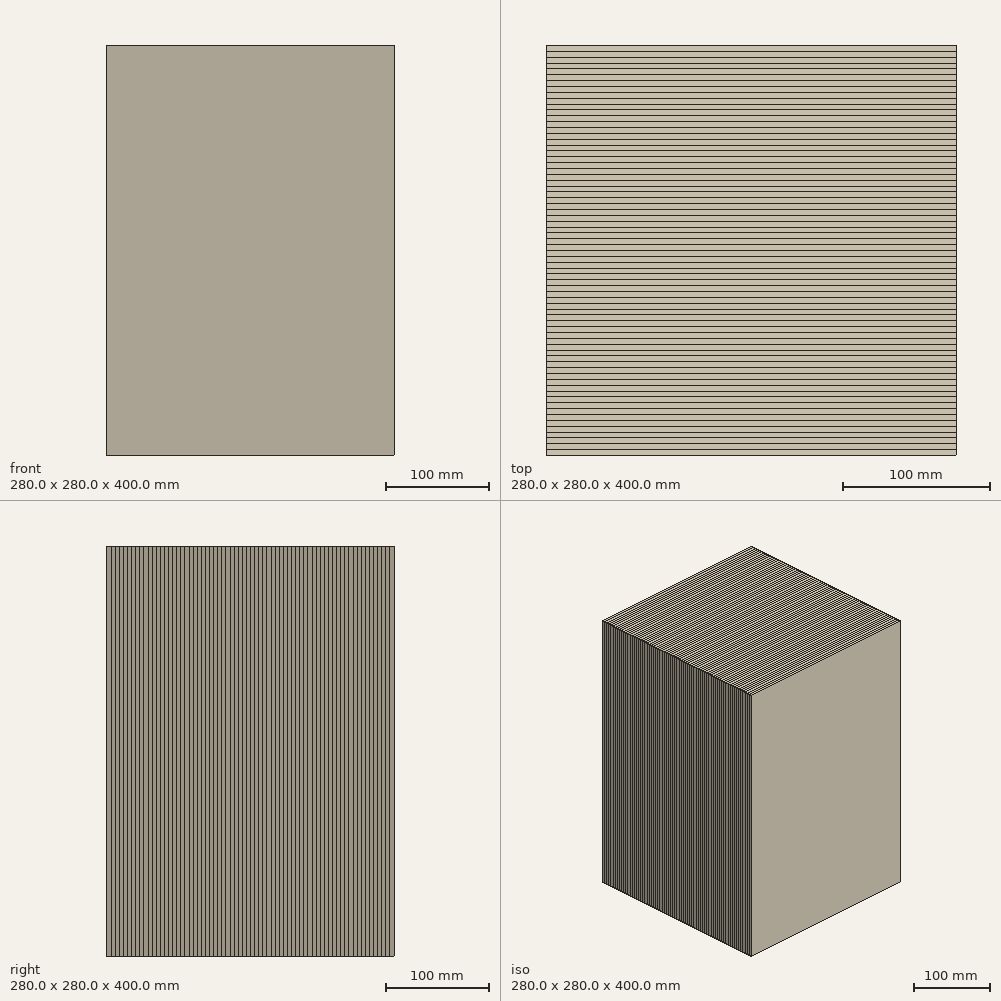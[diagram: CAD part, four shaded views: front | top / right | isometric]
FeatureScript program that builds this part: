
annotation { "Feature Type Name" : "Feature", "Feature Type Description" : "" }
export const myFeature = defineFeature(function(context is Context, id is Id, definition is map)
    precondition{}
    {
        {
            var Q0;
            Q0=qCreatedBy(makeId("Top.planeOp"),FACE);
            var sketch = newSketch(context, id + "F0", { "sketchPlane" : qUnion([Q0])});
            skLineSegment(sketch, "E0.bottom", {"start": v(-140, -140) * mm, "end": v(140, -140) * mm});
            skLineSegment(sketch, "E0.top", {"start": v(-140, 140) * mm, "end": v(140, 140) * mm});
            skLineSegment(sketch, "E0.left", {"start": v(-140, -140) * mm, "end": v(-140, 140) * mm});
            skLineSegment(sketch, "E0.right", {"start": v(140, -140) * mm, "end": v(140, 140) * mm});
            skPoint(sketch, "E0.middle", {"position": v(0, 0) * mm});
            skSolve(sketch);
        }
        {
            var Q0;
            Q0 = qSketchRegion(id + "F0", true);
            extrude(context, id + "F1", {"entities" : qUnion([Q0]), "depth" : 400 * mm, "offsetDistance" : 25 * mm});
        }
        {
            var Q0;
            Q0=makeQuery(id+"F1.opExtrude","SWEPT_FACE",FACE,{"disambiguationData":[OSD([sQuery(id+"F0.wireOp",EDGE,"E0.right")])]});
            var sketch = newSketch(context, id + "F2", { "sketchPlane" : qUnion([Q0])});
            skLineSegment(sketch, "E1.bottom", {"start": v(-140, 400) * mm, "end": v(-136, 400) * mm});
            skLineSegment(sketch, "E1.top", {"start": v(-140, 0) * mm, "end": v(-136, 0) * mm});
            skLineSegment(sketch, "E1.left", {"start": v(-140, 400) * mm, "end": v(-140, 0) * mm});
            skLineSegment(sketch, "E1.right", {"start": v(-136, 400) * mm, "end": v(-136, 0) * mm});
            skLineSegment(sketch, "E2.1.0.0", {"start": v(-132, 400) * mm, "end": v(-132, 0) * mm});
            skLineSegment(sketch, "E2.1.0.1", {"start": v(-128, 400) * mm, "end": v(-128, 0) * mm});
            skLineSegment(sketch, "E2.1.0.2", {"start": v(-132, 400) * mm, "end": v(-128, 400) * mm});
            skLineSegment(sketch, "E2.1.0.3", {"start": v(-132, 0) * mm, "end": v(-128, 0) * mm});
            skLineSegment(sketch, "E2.2.0.0", {"start": v(-124, 400) * mm, "end": v(-124, 0) * mm});
            skLineSegment(sketch, "E2.2.0.1", {"start": v(-120, 400) * mm, "end": v(-120, 0) * mm});
            skLineSegment(sketch, "E2.2.0.2", {"start": v(-124, 400) * mm, "end": v(-120, 400) * mm});
            skLineSegment(sketch, "E2.2.0.3", {"start": v(-124, 0) * mm, "end": v(-120, 0) * mm});
            skLineSegment(sketch, "E2.3.0.0", {"start": v(-116, 400) * mm, "end": v(-116, 0) * mm});
            skLineSegment(sketch, "E2.3.0.1", {"start": v(-112, 400) * mm, "end": v(-112, 0) * mm});
            skLineSegment(sketch, "E2.3.0.2", {"start": v(-116, 400) * mm, "end": v(-112, 400) * mm});
            skLineSegment(sketch, "E2.3.0.3", {"start": v(-116, 0) * mm, "end": v(-112, 0) * mm});
            skLineSegment(sketch, "E2.4.0.0", {"start": v(-108, 400) * mm, "end": v(-108, 0) * mm});
            skLineSegment(sketch, "E2.4.0.1", {"start": v(-104, 400) * mm, "end": v(-104, 0) * mm});
            skLineSegment(sketch, "E2.4.0.2", {"start": v(-108, 400) * mm, "end": v(-104, 400) * mm});
            skLineSegment(sketch, "E2.4.0.3", {"start": v(-108, 0) * mm, "end": v(-104, 0) * mm});
            skLineSegment(sketch, "E2.5.0.0", {"start": v(-100, 400) * mm, "end": v(-100, 0) * mm});
            skLineSegment(sketch, "E2.5.0.1", {"start": v(-96, 400) * mm, "end": v(-96, 0) * mm});
            skLineSegment(sketch, "E2.5.0.2", {"start": v(-100, 400) * mm, "end": v(-96, 400) * mm});
            skLineSegment(sketch, "E2.5.0.3", {"start": v(-100, 0) * mm, "end": v(-96, 0) * mm});
            skLineSegment(sketch, "E2.6.0.0", {"start": v(-92, 400) * mm, "end": v(-92, 0) * mm});
            skLineSegment(sketch, "E2.6.0.1", {"start": v(-88, 400) * mm, "end": v(-88, 0) * mm});
            skLineSegment(sketch, "E2.6.0.2", {"start": v(-92, 400) * mm, "end": v(-88, 400) * mm});
            skLineSegment(sketch, "E2.6.0.3", {"start": v(-92, 0) * mm, "end": v(-88, 0) * mm});
            skLineSegment(sketch, "E2.7.0.0", {"start": v(-84, 400) * mm, "end": v(-84, 0) * mm});
            skLineSegment(sketch, "E2.7.0.1", {"start": v(-80, 400) * mm, "end": v(-80, 0) * mm});
            skLineSegment(sketch, "E2.7.0.2", {"start": v(-84, 400) * mm, "end": v(-80, 400) * mm});
            skLineSegment(sketch, "E2.7.0.3", {"start": v(-84, 0) * mm, "end": v(-80, 0) * mm});
            skLineSegment(sketch, "E2.8.0.0", {"start": v(-76, 400) * mm, "end": v(-76, 0) * mm});
            skLineSegment(sketch, "E2.8.0.1", {"start": v(-72, 400) * mm, "end": v(-72, 0) * mm});
            skLineSegment(sketch, "E2.8.0.2", {"start": v(-76, 400) * mm, "end": v(-72, 400) * mm});
            skLineSegment(sketch, "E2.8.0.3", {"start": v(-76, 0) * mm, "end": v(-72, 0) * mm});
            skLineSegment(sketch, "E2.9.0.0", {"start": v(-68, 400) * mm, "end": v(-68, 0) * mm});
            skLineSegment(sketch, "E2.9.0.1", {"start": v(-64, 400) * mm, "end": v(-64, 0) * mm});
            skLineSegment(sketch, "E2.9.0.2", {"start": v(-68, 400) * mm, "end": v(-64, 400) * mm});
            skLineSegment(sketch, "E2.9.0.3", {"start": v(-68, 0) * mm, "end": v(-64, 0) * mm});
            skLineSegment(sketch, "E2.10.0.0", {"start": v(-60, 400) * mm, "end": v(-60, 0) * mm});
            skLineSegment(sketch, "E2.10.0.1", {"start": v(-56, 400) * mm, "end": v(-56, 0) * mm});
            skLineSegment(sketch, "E2.10.0.2", {"start": v(-60, 400) * mm, "end": v(-56, 400) * mm});
            skLineSegment(sketch, "E2.10.0.3", {"start": v(-60, 0) * mm, "end": v(-56, 0) * mm});
            skLineSegment(sketch, "E2.11.0.0", {"start": v(-52, 400) * mm, "end": v(-52, 0) * mm});
            skLineSegment(sketch, "E2.11.0.1", {"start": v(-48, 400) * mm, "end": v(-48, 0) * mm});
            skLineSegment(sketch, "E2.11.0.2", {"start": v(-52, 400) * mm, "end": v(-48, 400) * mm});
            skLineSegment(sketch, "E2.11.0.3", {"start": v(-52, 0) * mm, "end": v(-48, 0) * mm});
            skLineSegment(sketch, "E2.12.0.0", {"start": v(-44, 400) * mm, "end": v(-44, 0) * mm});
            skLineSegment(sketch, "E2.12.0.1", {"start": v(-40, 400) * mm, "end": v(-40, 0) * mm});
            skLineSegment(sketch, "E2.12.0.2", {"start": v(-44, 400) * mm, "end": v(-40, 400) * mm});
            skLineSegment(sketch, "E2.12.0.3", {"start": v(-44, 0) * mm, "end": v(-40, 0) * mm});
            skLineSegment(sketch, "E2.13.0.0", {"start": v(-36, 400) * mm, "end": v(-36, 0) * mm});
            skLineSegment(sketch, "E2.13.0.1", {"start": v(-32, 400) * mm, "end": v(-32, 0) * mm});
            skLineSegment(sketch, "E2.13.0.2", {"start": v(-36, 400) * mm, "end": v(-32, 400) * mm});
            skLineSegment(sketch, "E2.13.0.3", {"start": v(-36, 0) * mm, "end": v(-32, 0) * mm});
            skLineSegment(sketch, "E2.14.0.0", {"start": v(-28, 400) * mm, "end": v(-28, 0) * mm});
            skLineSegment(sketch, "E2.14.0.1", {"start": v(-24, 400) * mm, "end": v(-24, 0) * mm});
            skLineSegment(sketch, "E2.14.0.2", {"start": v(-28, 400) * mm, "end": v(-24, 400) * mm});
            skLineSegment(sketch, "E2.14.0.3", {"start": v(-28, 0) * mm, "end": v(-24, 0) * mm});
            skLineSegment(sketch, "E2.15.0.0", {"start": v(-20, 400) * mm, "end": v(-20, 0) * mm});
            skLineSegment(sketch, "E2.15.0.1", {"start": v(-16, 400) * mm, "end": v(-16, 0) * mm});
            skLineSegment(sketch, "E2.15.0.2", {"start": v(-20, 400) * mm, "end": v(-16, 400) * mm});
            skLineSegment(sketch, "E2.15.0.3", {"start": v(-20, 0) * mm, "end": v(-16, 0) * mm});
            skLineSegment(sketch, "E2.16.0.0", {"start": v(-12, 400) * mm, "end": v(-12, 0) * mm});
            skLineSegment(sketch, "E2.16.0.1", {"start": v(-8, 400) * mm, "end": v(-8, 0) * mm});
            skLineSegment(sketch, "E2.16.0.2", {"start": v(-12, 400) * mm, "end": v(-8, 400) * mm});
            skLineSegment(sketch, "E2.16.0.3", {"start": v(-12, 0) * mm, "end": v(-8, 0) * mm});
            skLineSegment(sketch, "E2.17.0.0", {"start": v(-4, 400) * mm, "end": v(-4, 0) * mm});
            skLineSegment(sketch, "E2.17.0.1", {"start": v(0, 400) * mm, "end": v(0, 0) * mm});
            skLineSegment(sketch, "E2.17.0.2", {"start": v(-4, 400) * mm, "end": v(0, 400) * mm});
            skLineSegment(sketch, "E2.17.0.3", {"start": v(-4, 0) * mm, "end": v(0, 0) * mm});
            skLineSegment(sketch, "E2.18.0.0", {"start": v(4, 400) * mm, "end": v(4, 0) * mm});
            skLineSegment(sketch, "E2.18.0.1", {"start": v(8, 400) * mm, "end": v(8, 0) * mm});
            skLineSegment(sketch, "E2.18.0.2", {"start": v(4, 400) * mm, "end": v(8, 400) * mm});
            skLineSegment(sketch, "E2.18.0.3", {"start": v(4, 0) * mm, "end": v(8, 0) * mm});
            skLineSegment(sketch, "E2.19.0.0", {"start": v(12, 400) * mm, "end": v(12, 0) * mm});
            skLineSegment(sketch, "E2.19.0.1", {"start": v(16, 400) * mm, "end": v(16, 0) * mm});
            skLineSegment(sketch, "E2.19.0.2", {"start": v(12, 400) * mm, "end": v(16, 400) * mm});
            skLineSegment(sketch, "E2.19.0.3", {"start": v(12, 0) * mm, "end": v(16, 0) * mm});
            skLineSegment(sketch, "E2.20.0.0", {"start": v(20, 400) * mm, "end": v(20, 0) * mm});
            skLineSegment(sketch, "E2.20.0.1", {"start": v(24, 400) * mm, "end": v(24, 0) * mm});
            skLineSegment(sketch, "E2.20.0.2", {"start": v(20, 400) * mm, "end": v(24, 400) * mm});
            skLineSegment(sketch, "E2.20.0.3", {"start": v(20, 0) * mm, "end": v(24, 0) * mm});
            skLineSegment(sketch, "E2.21.0.0", {"start": v(28, 400) * mm, "end": v(28, 0) * mm});
            skLineSegment(sketch, "E2.21.0.1", {"start": v(32, 400) * mm, "end": v(32, 0) * mm});
            skLineSegment(sketch, "E2.21.0.2", {"start": v(28, 400) * mm, "end": v(32, 400) * mm});
            skLineSegment(sketch, "E2.21.0.3", {"start": v(28, 0) * mm, "end": v(32, 0) * mm});
            skLineSegment(sketch, "E2.22.0.0", {"start": v(36, 400) * mm, "end": v(36, 0) * mm});
            skLineSegment(sketch, "E2.22.0.1", {"start": v(40, 400) * mm, "end": v(40, 0) * mm});
            skLineSegment(sketch, "E2.22.0.2", {"start": v(36, 400) * mm, "end": v(40, 400) * mm});
            skLineSegment(sketch, "E2.22.0.3", {"start": v(36, 0) * mm, "end": v(40, 0) * mm});
            skLineSegment(sketch, "E2.23.0.0", {"start": v(44, 400) * mm, "end": v(44, 0) * mm});
            skLineSegment(sketch, "E2.23.0.1", {"start": v(48, 400) * mm, "end": v(48, 0) * mm});
            skLineSegment(sketch, "E2.23.0.2", {"start": v(44, 400) * mm, "end": v(48, 400) * mm});
            skLineSegment(sketch, "E2.23.0.3", {"start": v(44, 0) * mm, "end": v(48, 0) * mm});
            skLineSegment(sketch, "E2.24.0.0", {"start": v(52, 400) * mm, "end": v(52, 0) * mm});
            skLineSegment(sketch, "E2.24.0.1", {"start": v(56, 400) * mm, "end": v(56, 0) * mm});
            skLineSegment(sketch, "E2.24.0.2", {"start": v(52, 400) * mm, "end": v(56, 400) * mm});
            skLineSegment(sketch, "E2.24.0.3", {"start": v(52, 0) * mm, "end": v(56, 0) * mm});
            skLineSegment(sketch, "E2.25.0.0", {"start": v(60, 400) * mm, "end": v(60, 0) * mm});
            skLineSegment(sketch, "E2.25.0.1", {"start": v(64, 400) * mm, "end": v(64, 0) * mm});
            skLineSegment(sketch, "E2.25.0.2", {"start": v(60, 400) * mm, "end": v(64, 400) * mm});
            skLineSegment(sketch, "E2.25.0.3", {"start": v(60, 0) * mm, "end": v(64, 0) * mm});
            skLineSegment(sketch, "E2.26.0.0", {"start": v(68, 400) * mm, "end": v(68, 0) * mm});
            skLineSegment(sketch, "E2.26.0.1", {"start": v(72, 400) * mm, "end": v(72, 0) * mm});
            skLineSegment(sketch, "E2.26.0.2", {"start": v(68, 400) * mm, "end": v(72, 400) * mm});
            skLineSegment(sketch, "E2.26.0.3", {"start": v(68, 0) * mm, "end": v(72, 0) * mm});
            skLineSegment(sketch, "E2.27.0.0", {"start": v(76, 400) * mm, "end": v(76, 0) * mm});
            skLineSegment(sketch, "E2.27.0.1", {"start": v(80, 400) * mm, "end": v(80, 0) * mm});
            skLineSegment(sketch, "E2.27.0.2", {"start": v(76, 400) * mm, "end": v(80, 400) * mm});
            skLineSegment(sketch, "E2.27.0.3", {"start": v(76, 0) * mm, "end": v(80, 0) * mm});
            skLineSegment(sketch, "E2.28.0.0", {"start": v(84, 400) * mm, "end": v(84, 0) * mm});
            skLineSegment(sketch, "E2.28.0.1", {"start": v(88, 400) * mm, "end": v(88, 0) * mm});
            skLineSegment(sketch, "E2.28.0.2", {"start": v(84, 400) * mm, "end": v(88, 400) * mm});
            skLineSegment(sketch, "E2.28.0.3", {"start": v(84, 0) * mm, "end": v(88, 0) * mm});
            skLineSegment(sketch, "E2.29.0.0", {"start": v(92, 400) * mm, "end": v(92, 0) * mm});
            skLineSegment(sketch, "E2.29.0.1", {"start": v(96, 400) * mm, "end": v(96, 0) * mm});
            skLineSegment(sketch, "E2.29.0.2", {"start": v(92, 400) * mm, "end": v(96, 400) * mm});
            skLineSegment(sketch, "E2.29.0.3", {"start": v(92, 0) * mm, "end": v(96, 0) * mm});
            skLineSegment(sketch, "E2.30.0.0", {"start": v(100, 400) * mm, "end": v(100, 0) * mm});
            skLineSegment(sketch, "E2.30.0.1", {"start": v(104, 400) * mm, "end": v(104, 0) * mm});
            skLineSegment(sketch, "E2.30.0.2", {"start": v(100, 400) * mm, "end": v(104, 400) * mm});
            skLineSegment(sketch, "E2.30.0.3", {"start": v(100, 0) * mm, "end": v(104, 0) * mm});
            skLineSegment(sketch, "E2.31.0.0", {"start": v(108, 400) * mm, "end": v(108, 0) * mm});
            skLineSegment(sketch, "E2.31.0.1", {"start": v(112, 400) * mm, "end": v(112, 0) * mm});
            skLineSegment(sketch, "E2.31.0.2", {"start": v(108, 400) * mm, "end": v(112, 400) * mm});
            skLineSegment(sketch, "E2.31.0.3", {"start": v(108, 0) * mm, "end": v(112, 0) * mm});
            skLineSegment(sketch, "E2.32.0.0", {"start": v(116, 400) * mm, "end": v(116, 0) * mm});
            skLineSegment(sketch, "E2.32.0.1", {"start": v(120, 400) * mm, "end": v(120, 0) * mm});
            skLineSegment(sketch, "E2.32.0.2", {"start": v(116, 400) * mm, "end": v(120, 400) * mm});
            skLineSegment(sketch, "E2.32.0.3", {"start": v(116, 0) * mm, "end": v(120, 0) * mm});
            skLineSegment(sketch, "E2.33.0.0", {"start": v(124, 400) * mm, "end": v(124, 0) * mm});
            skLineSegment(sketch, "E2.33.0.1", {"start": v(128, 400) * mm, "end": v(128, 0) * mm});
            skLineSegment(sketch, "E2.33.0.2", {"start": v(124, 400) * mm, "end": v(128, 400) * mm});
            skLineSegment(sketch, "E2.33.0.3", {"start": v(124, 0) * mm, "end": v(128, 0) * mm});
            skLineSegment(sketch, "E2.34.0.0", {"start": v(132, 400) * mm, "end": v(132, 0) * mm});
            skLineSegment(sketch, "E2.34.0.1", {"start": v(136, 400) * mm, "end": v(136, 0) * mm});
            skLineSegment(sketch, "E2.34.0.2", {"start": v(132, 400) * mm, "end": v(136, 400) * mm});
            skLineSegment(sketch, "E2.34.0.3", {"start": v(132, 0) * mm, "end": v(136, 0) * mm});
            skLineSegment(sketch, "E2.direction1", {"start": v(-140, 0) * mm, "end": v(-132, 0) * mm, "construction": true});
            skSolve(sketch);
        }
        {
            var Q0;
            Q0 = qSketchRegion(id + "F2", true);
            extrude(context, id + "F3", {"entities" : qUnion([Q0]), "operationType" : NewBodyOperationType.REMOVE, "oppositeDirection" : true, "depth" : 0.01 * mm, "offsetDistance" : 25 * mm});
        }
        {
            var Q0;
            Q0=makeQuery(id+"F1.opExtrude","SWEPT_FACE",FACE,{"disambiguationData":[OSD([sQuery(id+"F0.wireOp",EDGE,"E0.left")])]});
            var sketch = newSketch(context, id + "F4", { "sketchPlane" : qUnion([Q0])});
            skLineSegment(sketch, "E3.bottom", {"start": v(-140, 400) * mm, "end": v(-136, 400) * mm});
            skLineSegment(sketch, "E3.top", {"start": v(-140, 0) * mm, "end": v(-136, 0) * mm});
            skLineSegment(sketch, "E3.left", {"start": v(-140, 400) * mm, "end": v(-140, 0) * mm});
            skLineSegment(sketch, "E3.right", {"start": v(-136, 400) * mm, "end": v(-136, 0) * mm});
            skLineSegment(sketch, "E4.1.0.0", {"start": v(-132, 400) * mm, "end": v(-128, 400) * mm});
            skLineSegment(sketch, "E4.1.0.1", {"start": v(-132, 400) * mm, "end": v(-132, 0) * mm});
            skLineSegment(sketch, "E4.1.0.2", {"start": v(-128, 400) * mm, "end": v(-128, 0) * mm});
            skLineSegment(sketch, "E4.1.0.3", {"start": v(-132, 0) * mm, "end": v(-128, 0) * mm});
            skLineSegment(sketch, "E4.2.0.0", {"start": v(-124, 400) * mm, "end": v(-120, 400) * mm});
            skLineSegment(sketch, "E4.2.0.1", {"start": v(-124, 400) * mm, "end": v(-124, 0) * mm});
            skLineSegment(sketch, "E4.2.0.2", {"start": v(-120, 400) * mm, "end": v(-120, 0) * mm});
            skLineSegment(sketch, "E4.2.0.3", {"start": v(-124, 0) * mm, "end": v(-120, 0) * mm});
            skLineSegment(sketch, "E4.3.0.0", {"start": v(-116, 400) * mm, "end": v(-112, 400) * mm});
            skLineSegment(sketch, "E4.3.0.1", {"start": v(-116, 400) * mm, "end": v(-116, 0) * mm});
            skLineSegment(sketch, "E4.3.0.2", {"start": v(-112, 400) * mm, "end": v(-112, 0) * mm});
            skLineSegment(sketch, "E4.3.0.3", {"start": v(-116, 0) * mm, "end": v(-112, 0) * mm});
            skLineSegment(sketch, "E4.4.0.0", {"start": v(-108, 400) * mm, "end": v(-104, 400) * mm});
            skLineSegment(sketch, "E4.4.0.1", {"start": v(-108, 400) * mm, "end": v(-108, 0) * mm});
            skLineSegment(sketch, "E4.4.0.2", {"start": v(-104, 400) * mm, "end": v(-104, 0) * mm});
            skLineSegment(sketch, "E4.4.0.3", {"start": v(-108, 0) * mm, "end": v(-104, 0) * mm});
            skLineSegment(sketch, "E4.5.0.0", {"start": v(-100, 400) * mm, "end": v(-96, 400) * mm});
            skLineSegment(sketch, "E4.5.0.1", {"start": v(-100, 400) * mm, "end": v(-100, 0) * mm});
            skLineSegment(sketch, "E4.5.0.2", {"start": v(-96, 400) * mm, "end": v(-96, 0) * mm});
            skLineSegment(sketch, "E4.5.0.3", {"start": v(-100, 0) * mm, "end": v(-96, 0) * mm});
            skLineSegment(sketch, "E4.6.0.0", {"start": v(-92, 400) * mm, "end": v(-88, 400) * mm});
            skLineSegment(sketch, "E4.6.0.1", {"start": v(-92, 400) * mm, "end": v(-92, 0) * mm});
            skLineSegment(sketch, "E4.6.0.2", {"start": v(-88, 400) * mm, "end": v(-88, 0) * mm});
            skLineSegment(sketch, "E4.6.0.3", {"start": v(-92, 0) * mm, "end": v(-88, 0) * mm});
            skLineSegment(sketch, "E4.7.0.0", {"start": v(-84, 400) * mm, "end": v(-80, 400) * mm});
            skLineSegment(sketch, "E4.7.0.1", {"start": v(-84, 400) * mm, "end": v(-84, 0) * mm});
            skLineSegment(sketch, "E4.7.0.2", {"start": v(-80, 400) * mm, "end": v(-80, 0) * mm});
            skLineSegment(sketch, "E4.7.0.3", {"start": v(-84, 0) * mm, "end": v(-80, 0) * mm});
            skLineSegment(sketch, "E4.8.0.0", {"start": v(-76, 400) * mm, "end": v(-72, 400) * mm});
            skLineSegment(sketch, "E4.8.0.1", {"start": v(-76, 400) * mm, "end": v(-76, 0) * mm});
            skLineSegment(sketch, "E4.8.0.2", {"start": v(-72, 400) * mm, "end": v(-72, 0) * mm});
            skLineSegment(sketch, "E4.8.0.3", {"start": v(-76, 0) * mm, "end": v(-72, 0) * mm});
            skLineSegment(sketch, "E4.9.0.0", {"start": v(-68, 400) * mm, "end": v(-64, 400) * mm});
            skLineSegment(sketch, "E4.9.0.1", {"start": v(-68, 400) * mm, "end": v(-68, 0) * mm});
            skLineSegment(sketch, "E4.9.0.2", {"start": v(-64, 400) * mm, "end": v(-64, 0) * mm});
            skLineSegment(sketch, "E4.9.0.3", {"start": v(-68, 0) * mm, "end": v(-64, 0) * mm});
            skLineSegment(sketch, "E4.10.0.0", {"start": v(-60, 400) * mm, "end": v(-56, 400) * mm});
            skLineSegment(sketch, "E4.10.0.1", {"start": v(-60, 400) * mm, "end": v(-60, 0) * mm});
            skLineSegment(sketch, "E4.10.0.2", {"start": v(-56, 400) * mm, "end": v(-56, 0) * mm});
            skLineSegment(sketch, "E4.10.0.3", {"start": v(-60, 0) * mm, "end": v(-56, 0) * mm});
            skLineSegment(sketch, "E4.11.0.0", {"start": v(-52, 400) * mm, "end": v(-48, 400) * mm});
            skLineSegment(sketch, "E4.11.0.1", {"start": v(-52, 400) * mm, "end": v(-52, 0) * mm});
            skLineSegment(sketch, "E4.11.0.2", {"start": v(-48, 400) * mm, "end": v(-48, 0) * mm});
            skLineSegment(sketch, "E4.11.0.3", {"start": v(-52, 0) * mm, "end": v(-48, 0) * mm});
            skLineSegment(sketch, "E4.12.0.0", {"start": v(-44, 400) * mm, "end": v(-40, 400) * mm});
            skLineSegment(sketch, "E4.12.0.1", {"start": v(-44, 400) * mm, "end": v(-44, 0) * mm});
            skLineSegment(sketch, "E4.12.0.2", {"start": v(-40, 400) * mm, "end": v(-40, 0) * mm});
            skLineSegment(sketch, "E4.12.0.3", {"start": v(-44, 0) * mm, "end": v(-40, 0) * mm});
            skLineSegment(sketch, "E4.13.0.0", {"start": v(-36, 400) * mm, "end": v(-32, 400) * mm});
            skLineSegment(sketch, "E4.13.0.1", {"start": v(-36, 400) * mm, "end": v(-36, 0) * mm});
            skLineSegment(sketch, "E4.13.0.2", {"start": v(-32, 400) * mm, "end": v(-32, 0) * mm});
            skLineSegment(sketch, "E4.13.0.3", {"start": v(-36, 0) * mm, "end": v(-32, 0) * mm});
            skLineSegment(sketch, "E4.14.0.0", {"start": v(-28, 400) * mm, "end": v(-24, 400) * mm});
            skLineSegment(sketch, "E4.14.0.1", {"start": v(-28, 400) * mm, "end": v(-28, 0) * mm});
            skLineSegment(sketch, "E4.14.0.2", {"start": v(-24, 400) * mm, "end": v(-24, 0) * mm});
            skLineSegment(sketch, "E4.14.0.3", {"start": v(-28, 0) * mm, "end": v(-24, 0) * mm});
            skLineSegment(sketch, "E4.15.0.0", {"start": v(-20, 400) * mm, "end": v(-16, 400) * mm});
            skLineSegment(sketch, "E4.15.0.1", {"start": v(-20, 400) * mm, "end": v(-20, 0) * mm});
            skLineSegment(sketch, "E4.15.0.2", {"start": v(-16, 400) * mm, "end": v(-16, 0) * mm});
            skLineSegment(sketch, "E4.15.0.3", {"start": v(-20, 0) * mm, "end": v(-16, 0) * mm});
            skLineSegment(sketch, "E4.16.0.0", {"start": v(-12, 400) * mm, "end": v(-8, 400) * mm});
            skLineSegment(sketch, "E4.16.0.1", {"start": v(-12, 400) * mm, "end": v(-12, 0) * mm});
            skLineSegment(sketch, "E4.16.0.2", {"start": v(-8, 400) * mm, "end": v(-8, 0) * mm});
            skLineSegment(sketch, "E4.16.0.3", {"start": v(-12, 0) * mm, "end": v(-8, 0) * mm});
            skLineSegment(sketch, "E4.17.0.0", {"start": v(-4, 400) * mm, "end": v(0, 400) * mm});
            skLineSegment(sketch, "E4.17.0.1", {"start": v(-4, 400) * mm, "end": v(-4, 0) * mm});
            skLineSegment(sketch, "E4.17.0.2", {"start": v(0, 400) * mm, "end": v(0, 0) * mm});
            skLineSegment(sketch, "E4.17.0.3", {"start": v(-4, 0) * mm, "end": v(0, 0) * mm});
            skLineSegment(sketch, "E4.18.0.0", {"start": v(4, 400) * mm, "end": v(8, 400) * mm});
            skLineSegment(sketch, "E4.18.0.1", {"start": v(4, 400) * mm, "end": v(4, 0) * mm});
            skLineSegment(sketch, "E4.18.0.2", {"start": v(8, 400) * mm, "end": v(8, 0) * mm});
            skLineSegment(sketch, "E4.18.0.3", {"start": v(4, 0) * mm, "end": v(8, 0) * mm});
            skLineSegment(sketch, "E4.19.0.0", {"start": v(12, 400) * mm, "end": v(16, 400) * mm});
            skLineSegment(sketch, "E4.19.0.1", {"start": v(12, 400) * mm, "end": v(12, 0) * mm});
            skLineSegment(sketch, "E4.19.0.2", {"start": v(16, 400) * mm, "end": v(16, 0) * mm});
            skLineSegment(sketch, "E4.19.0.3", {"start": v(12, 0) * mm, "end": v(16, 0) * mm});
            skLineSegment(sketch, "E4.20.0.0", {"start": v(20, 400) * mm, "end": v(24, 400) * mm});
            skLineSegment(sketch, "E4.20.0.1", {"start": v(20, 400) * mm, "end": v(20, 0) * mm});
            skLineSegment(sketch, "E4.20.0.2", {"start": v(24, 400) * mm, "end": v(24, 0) * mm});
            skLineSegment(sketch, "E4.20.0.3", {"start": v(20, 0) * mm, "end": v(24, 0) * mm});
            skLineSegment(sketch, "E4.21.0.0", {"start": v(28, 400) * mm, "end": v(32, 400) * mm});
            skLineSegment(sketch, "E4.21.0.1", {"start": v(28, 400) * mm, "end": v(28, 0) * mm});
            skLineSegment(sketch, "E4.21.0.2", {"start": v(32, 400) * mm, "end": v(32, 0) * mm});
            skLineSegment(sketch, "E4.21.0.3", {"start": v(28, 0) * mm, "end": v(32, 0) * mm});
            skLineSegment(sketch, "E4.22.0.0", {"start": v(36, 400) * mm, "end": v(40, 400) * mm});
            skLineSegment(sketch, "E4.22.0.1", {"start": v(36, 400) * mm, "end": v(36, 0) * mm});
            skLineSegment(sketch, "E4.22.0.2", {"start": v(40, 400) * mm, "end": v(40, 0) * mm});
            skLineSegment(sketch, "E4.22.0.3", {"start": v(36, 0) * mm, "end": v(40, 0) * mm});
            skLineSegment(sketch, "E4.23.0.0", {"start": v(44, 400) * mm, "end": v(48, 400) * mm});
            skLineSegment(sketch, "E4.23.0.1", {"start": v(44, 400) * mm, "end": v(44, 0) * mm});
            skLineSegment(sketch, "E4.23.0.2", {"start": v(48, 400) * mm, "end": v(48, 0) * mm});
            skLineSegment(sketch, "E4.23.0.3", {"start": v(44, 0) * mm, "end": v(48, 0) * mm});
            skLineSegment(sketch, "E4.24.0.0", {"start": v(52, 400) * mm, "end": v(56, 400) * mm});
            skLineSegment(sketch, "E4.24.0.1", {"start": v(52, 400) * mm, "end": v(52, 0) * mm});
            skLineSegment(sketch, "E4.24.0.2", {"start": v(56, 400) * mm, "end": v(56, 0) * mm});
            skLineSegment(sketch, "E4.24.0.3", {"start": v(52, 0) * mm, "end": v(56, 0) * mm});
            skLineSegment(sketch, "E4.25.0.0", {"start": v(60, 400) * mm, "end": v(64, 400) * mm});
            skLineSegment(sketch, "E4.25.0.1", {"start": v(60, 400) * mm, "end": v(60, 0) * mm});
            skLineSegment(sketch, "E4.25.0.2", {"start": v(64, 400) * mm, "end": v(64, 0) * mm});
            skLineSegment(sketch, "E4.25.0.3", {"start": v(60, 0) * mm, "end": v(64, 0) * mm});
            skLineSegment(sketch, "E4.26.0.0", {"start": v(68, 400) * mm, "end": v(72, 400) * mm});
            skLineSegment(sketch, "E4.26.0.1", {"start": v(68, 400) * mm, "end": v(68, 0) * mm});
            skLineSegment(sketch, "E4.26.0.2", {"start": v(72, 400) * mm, "end": v(72, 0) * mm});
            skLineSegment(sketch, "E4.26.0.3", {"start": v(68, 0) * mm, "end": v(72, 0) * mm});
            skLineSegment(sketch, "E4.27.0.0", {"start": v(76, 400) * mm, "end": v(80, 400) * mm});
            skLineSegment(sketch, "E4.27.0.1", {"start": v(76, 400) * mm, "end": v(76, 0) * mm});
            skLineSegment(sketch, "E4.27.0.2", {"start": v(80, 400) * mm, "end": v(80, 0) * mm});
            skLineSegment(sketch, "E4.27.0.3", {"start": v(76, 0) * mm, "end": v(80, 0) * mm});
            skLineSegment(sketch, "E4.28.0.0", {"start": v(84, 400) * mm, "end": v(88, 400) * mm});
            skLineSegment(sketch, "E4.28.0.1", {"start": v(84, 400) * mm, "end": v(84, 0) * mm});
            skLineSegment(sketch, "E4.28.0.2", {"start": v(88, 400) * mm, "end": v(88, 0) * mm});
            skLineSegment(sketch, "E4.28.0.3", {"start": v(84, 0) * mm, "end": v(88, 0) * mm});
            skLineSegment(sketch, "E4.29.0.0", {"start": v(92, 400) * mm, "end": v(96, 400) * mm});
            skLineSegment(sketch, "E4.29.0.1", {"start": v(92, 400) * mm, "end": v(92, 0) * mm});
            skLineSegment(sketch, "E4.29.0.2", {"start": v(96, 400) * mm, "end": v(96, 0) * mm});
            skLineSegment(sketch, "E4.29.0.3", {"start": v(92, 0) * mm, "end": v(96, 0) * mm});
            skLineSegment(sketch, "E4.30.0.0", {"start": v(100, 400) * mm, "end": v(104, 400) * mm});
            skLineSegment(sketch, "E4.30.0.1", {"start": v(100, 400) * mm, "end": v(100, 0) * mm});
            skLineSegment(sketch, "E4.30.0.2", {"start": v(104, 400) * mm, "end": v(104, 0) * mm});
            skLineSegment(sketch, "E4.30.0.3", {"start": v(100, 0) * mm, "end": v(104, 0) * mm});
            skLineSegment(sketch, "E4.31.0.0", {"start": v(108, 400) * mm, "end": v(112, 400) * mm});
            skLineSegment(sketch, "E4.31.0.1", {"start": v(108, 400) * mm, "end": v(108, 0) * mm});
            skLineSegment(sketch, "E4.31.0.2", {"start": v(112, 400) * mm, "end": v(112, 0) * mm});
            skLineSegment(sketch, "E4.31.0.3", {"start": v(108, 0) * mm, "end": v(112, 0) * mm});
            skLineSegment(sketch, "E4.32.0.0", {"start": v(116, 400) * mm, "end": v(120, 400) * mm});
            skLineSegment(sketch, "E4.32.0.1", {"start": v(116, 400) * mm, "end": v(116, 0) * mm});
            skLineSegment(sketch, "E4.32.0.2", {"start": v(120, 400) * mm, "end": v(120, 0) * mm});
            skLineSegment(sketch, "E4.32.0.3", {"start": v(116, 0) * mm, "end": v(120, 0) * mm});
            skLineSegment(sketch, "E4.33.0.0", {"start": v(124, 400) * mm, "end": v(128, 400) * mm});
            skLineSegment(sketch, "E4.33.0.1", {"start": v(124, 400) * mm, "end": v(124, 0) * mm});
            skLineSegment(sketch, "E4.33.0.2", {"start": v(128, 400) * mm, "end": v(128, 0) * mm});
            skLineSegment(sketch, "E4.33.0.3", {"start": v(124, 0) * mm, "end": v(128, 0) * mm});
            skLineSegment(sketch, "E4.34.0.0", {"start": v(132, 400) * mm, "end": v(136, 400) * mm});
            skLineSegment(sketch, "E4.34.0.1", {"start": v(132, 400) * mm, "end": v(132, 0) * mm});
            skLineSegment(sketch, "E4.34.0.2", {"start": v(136, 400) * mm, "end": v(136, 0) * mm});
            skLineSegment(sketch, "E4.34.0.3", {"start": v(132, 0) * mm, "end": v(136, 0) * mm});
            skLineSegment(sketch, "E4.direction1", {"start": v(-140, 400) * mm, "end": v(-132, 400) * mm, "construction": true});
            skSolve(sketch);
        }
        {
            var Q0;
            Q0 = qSketchRegion(id + "F4", true);
            extrude(context, id + "F5", {"entities" : qUnion([Q0]), "operationType" : NewBodyOperationType.REMOVE, "oppositeDirection" : true, "depth" : 0.01 * mm, "offsetDistance" : 25 * mm});
        }
        {
            var Q0;
            Q0=makeQuery(id+"F1.opExtrude","CAP_FACE",FACE,{"disambiguationData":[OSD([sQuery(id+"F0.wireOp",EDGE,"E0.bottom"),sQuery(id+"F0.wireOp",EDGE,"E0.top"),sQuery(id+"F0.wireOp",EDGE,"E0.left"),sQuery(id+"F0.wireOp",EDGE,"E0.right")])],"isStart":false});
            var sketch = newSketch(context, id + "F6", { "sketchPlane" : qUnion([Q0])});
            skLineSegment(sketch, "E5.bottom", {"start": v(-140, -140) * mm, "end": v(140, -140) * mm});
            skLineSegment(sketch, "E5.top", {"start": v(-140, -136) * mm, "end": v(140, -136) * mm});
            skLineSegment(sketch, "E5.left", {"start": v(-140, -140) * mm, "end": v(-140, -136) * mm});
            skLineSegment(sketch, "E5.right", {"start": v(140, -140) * mm, "end": v(140, -136) * mm});
            skLineSegment(sketch, "E6.0.1.0", {"start": v(-140, -128) * mm, "end": v(140, -128) * mm});
            skLineSegment(sketch, "E6.0.1.1", {"start": v(-140, -132) * mm, "end": v(-140, -128) * mm});
            skLineSegment(sketch, "E6.0.1.2", {"start": v(-140, -132) * mm, "end": v(140, -132) * mm});
            skLineSegment(sketch, "E6.0.1.3", {"start": v(140, -132) * mm, "end": v(140, -128) * mm});
            skLineSegment(sketch, "E6.0.2.0", {"start": v(-140, -120) * mm, "end": v(140, -120) * mm});
            skLineSegment(sketch, "E6.0.2.1", {"start": v(-140, -124) * mm, "end": v(-140, -120) * mm});
            skLineSegment(sketch, "E6.0.2.2", {"start": v(-140, -124) * mm, "end": v(140, -124) * mm});
            skLineSegment(sketch, "E6.0.2.3", {"start": v(140, -124) * mm, "end": v(140, -120) * mm});
            skLineSegment(sketch, "E6.0.3.0", {"start": v(-140, -112) * mm, "end": v(140, -112) * mm});
            skLineSegment(sketch, "E6.0.3.1", {"start": v(-140, -116) * mm, "end": v(-140, -112) * mm});
            skLineSegment(sketch, "E6.0.3.2", {"start": v(-140, -116) * mm, "end": v(140, -116) * mm});
            skLineSegment(sketch, "E6.0.3.3", {"start": v(140, -116) * mm, "end": v(140, -112) * mm});
            skLineSegment(sketch, "E6.0.4.0", {"start": v(-140, -104) * mm, "end": v(140, -104) * mm});
            skLineSegment(sketch, "E6.0.4.1", {"start": v(-140, -108) * mm, "end": v(-140, -104) * mm});
            skLineSegment(sketch, "E6.0.4.2", {"start": v(-140, -108) * mm, "end": v(140, -108) * mm});
            skLineSegment(sketch, "E6.0.4.3", {"start": v(140, -108) * mm, "end": v(140, -104) * mm});
            skLineSegment(sketch, "E6.0.5.0", {"start": v(-140, -96) * mm, "end": v(140, -96) * mm});
            skLineSegment(sketch, "E6.0.5.1", {"start": v(-140, -100) * mm, "end": v(-140, -96) * mm});
            skLineSegment(sketch, "E6.0.5.2", {"start": v(-140, -100) * mm, "end": v(140, -100) * mm});
            skLineSegment(sketch, "E6.0.5.3", {"start": v(140, -100) * mm, "end": v(140, -96) * mm});
            skLineSegment(sketch, "E6.0.6.0", {"start": v(-140, -88) * mm, "end": v(140, -88) * mm});
            skLineSegment(sketch, "E6.0.6.1", {"start": v(-140, -92) * mm, "end": v(-140, -88) * mm});
            skLineSegment(sketch, "E6.0.6.2", {"start": v(-140, -92) * mm, "end": v(140, -92) * mm});
            skLineSegment(sketch, "E6.0.6.3", {"start": v(140, -92) * mm, "end": v(140, -88) * mm});
            skLineSegment(sketch, "E6.0.7.0", {"start": v(-140, -80) * mm, "end": v(140, -80) * mm});
            skLineSegment(sketch, "E6.0.7.1", {"start": v(-140, -84) * mm, "end": v(-140, -80) * mm});
            skLineSegment(sketch, "E6.0.7.2", {"start": v(-140, -84) * mm, "end": v(140, -84) * mm});
            skLineSegment(sketch, "E6.0.7.3", {"start": v(140, -84) * mm, "end": v(140, -80) * mm});
            skLineSegment(sketch, "E6.0.8.0", {"start": v(-140, -72) * mm, "end": v(140, -72) * mm});
            skLineSegment(sketch, "E6.0.8.1", {"start": v(-140, -76) * mm, "end": v(-140, -72) * mm});
            skLineSegment(sketch, "E6.0.8.2", {"start": v(-140, -76) * mm, "end": v(140, -76) * mm});
            skLineSegment(sketch, "E6.0.8.3", {"start": v(140, -76) * mm, "end": v(140, -72) * mm});
            skLineSegment(sketch, "E6.0.9.0", {"start": v(-140, -64) * mm, "end": v(140, -64) * mm});
            skLineSegment(sketch, "E6.0.9.1", {"start": v(-140, -68) * mm, "end": v(-140, -64) * mm});
            skLineSegment(sketch, "E6.0.9.2", {"start": v(-140, -68) * mm, "end": v(140, -68) * mm});
            skLineSegment(sketch, "E6.0.9.3", {"start": v(140, -68) * mm, "end": v(140, -64) * mm});
            skLineSegment(sketch, "E6.0.10.0", {"start": v(-140, -56) * mm, "end": v(140, -56) * mm});
            skLineSegment(sketch, "E6.0.10.1", {"start": v(-140, -60) * mm, "end": v(-140, -56) * mm});
            skLineSegment(sketch, "E6.0.10.2", {"start": v(-140, -60) * mm, "end": v(140, -60) * mm});
            skLineSegment(sketch, "E6.0.10.3", {"start": v(140, -60) * mm, "end": v(140, -56) * mm});
            skLineSegment(sketch, "E6.0.11.0", {"start": v(-140, -48) * mm, "end": v(140, -48) * mm});
            skLineSegment(sketch, "E6.0.11.1", {"start": v(-140, -52) * mm, "end": v(-140, -48) * mm});
            skLineSegment(sketch, "E6.0.11.2", {"start": v(-140, -52) * mm, "end": v(140, -52) * mm});
            skLineSegment(sketch, "E6.0.11.3", {"start": v(140, -52) * mm, "end": v(140, -48) * mm});
            skLineSegment(sketch, "E6.0.12.0", {"start": v(-140, -40) * mm, "end": v(140, -40) * mm});
            skLineSegment(sketch, "E6.0.12.1", {"start": v(-140, -44) * mm, "end": v(-140, -40) * mm});
            skLineSegment(sketch, "E6.0.12.2", {"start": v(-140, -44) * mm, "end": v(140, -44) * mm});
            skLineSegment(sketch, "E6.0.12.3", {"start": v(140, -44) * mm, "end": v(140, -40) * mm});
            skLineSegment(sketch, "E6.0.13.0", {"start": v(-140, -32) * mm, "end": v(140, -32) * mm});
            skLineSegment(sketch, "E6.0.13.1", {"start": v(-140, -36) * mm, "end": v(-140, -32) * mm});
            skLineSegment(sketch, "E6.0.13.2", {"start": v(-140, -36) * mm, "end": v(140, -36) * mm});
            skLineSegment(sketch, "E6.0.13.3", {"start": v(140, -36) * mm, "end": v(140, -32) * mm});
            skLineSegment(sketch, "E6.0.14.0", {"start": v(-140, -24) * mm, "end": v(140, -24) * mm});
            skLineSegment(sketch, "E6.0.14.1", {"start": v(-140, -28) * mm, "end": v(-140, -24) * mm});
            skLineSegment(sketch, "E6.0.14.2", {"start": v(-140, -28) * mm, "end": v(140, -28) * mm});
            skLineSegment(sketch, "E6.0.14.3", {"start": v(140, -28) * mm, "end": v(140, -24) * mm});
            skLineSegment(sketch, "E6.0.15.0", {"start": v(-140, -16) * mm, "end": v(140, -16) * mm});
            skLineSegment(sketch, "E6.0.15.1", {"start": v(-140, -20) * mm, "end": v(-140, -16) * mm});
            skLineSegment(sketch, "E6.0.15.2", {"start": v(-140, -20) * mm, "end": v(140, -20) * mm});
            skLineSegment(sketch, "E6.0.15.3", {"start": v(140, -20) * mm, "end": v(140, -16) * mm});
            skLineSegment(sketch, "E6.0.16.0", {"start": v(-140, -8) * mm, "end": v(140, -8) * mm});
            skLineSegment(sketch, "E6.0.16.1", {"start": v(-140, -12) * mm, "end": v(-140, -8) * mm});
            skLineSegment(sketch, "E6.0.16.2", {"start": v(-140, -12) * mm, "end": v(140, -12) * mm});
            skLineSegment(sketch, "E6.0.16.3", {"start": v(140, -12) * mm, "end": v(140, -8) * mm});
            skLineSegment(sketch, "E6.0.17.0", {"start": v(-140, 0) * mm, "end": v(140, 0) * mm});
            skLineSegment(sketch, "E6.0.17.1", {"start": v(-140, -4) * mm, "end": v(-140, 0) * mm});
            skLineSegment(sketch, "E6.0.17.2", {"start": v(-140, -4) * mm, "end": v(140, -4) * mm});
            skLineSegment(sketch, "E6.0.17.3", {"start": v(140, -4) * mm, "end": v(140, 0) * mm});
            skLineSegment(sketch, "E6.0.18.0", {"start": v(-140, 8) * mm, "end": v(140, 8) * mm});
            skLineSegment(sketch, "E6.0.18.1", {"start": v(-140, 4) * mm, "end": v(-140, 8) * mm});
            skLineSegment(sketch, "E6.0.18.2", {"start": v(-140, 4) * mm, "end": v(140, 4) * mm});
            skLineSegment(sketch, "E6.0.18.3", {"start": v(140, 4) * mm, "end": v(140, 8) * mm});
            skLineSegment(sketch, "E6.0.19.0", {"start": v(-140, 16) * mm, "end": v(140, 16) * mm});
            skLineSegment(sketch, "E6.0.19.1", {"start": v(-140, 12) * mm, "end": v(-140, 16) * mm});
            skLineSegment(sketch, "E6.0.19.2", {"start": v(-140, 12) * mm, "end": v(140, 12) * mm});
            skLineSegment(sketch, "E6.0.19.3", {"start": v(140, 12) * mm, "end": v(140, 16) * mm});
            skLineSegment(sketch, "E6.0.20.0", {"start": v(-140, 24) * mm, "end": v(140, 24) * mm});
            skLineSegment(sketch, "E6.0.20.1", {"start": v(-140, 20) * mm, "end": v(-140, 24) * mm});
            skLineSegment(sketch, "E6.0.20.2", {"start": v(-140, 20) * mm, "end": v(140, 20) * mm});
            skLineSegment(sketch, "E6.0.20.3", {"start": v(140, 20) * mm, "end": v(140, 24) * mm});
            skLineSegment(sketch, "E6.0.21.0", {"start": v(-140, 32) * mm, "end": v(140, 32) * mm});
            skLineSegment(sketch, "E6.0.21.1", {"start": v(-140, 28) * mm, "end": v(-140, 32) * mm});
            skLineSegment(sketch, "E6.0.21.2", {"start": v(-140, 28) * mm, "end": v(140, 28) * mm});
            skLineSegment(sketch, "E6.0.21.3", {"start": v(140, 28) * mm, "end": v(140, 32) * mm});
            skLineSegment(sketch, "E6.0.22.0", {"start": v(-140, 40) * mm, "end": v(140, 40) * mm});
            skLineSegment(sketch, "E6.0.22.1", {"start": v(-140, 36) * mm, "end": v(-140, 40) * mm});
            skLineSegment(sketch, "E6.0.22.2", {"start": v(-140, 36) * mm, "end": v(140, 36) * mm});
            skLineSegment(sketch, "E6.0.22.3", {"start": v(140, 36) * mm, "end": v(140, 40) * mm});
            skLineSegment(sketch, "E6.0.23.0", {"start": v(-140, 48) * mm, "end": v(140, 48) * mm});
            skLineSegment(sketch, "E6.0.23.1", {"start": v(-140, 44) * mm, "end": v(-140, 48) * mm});
            skLineSegment(sketch, "E6.0.23.2", {"start": v(-140, 44) * mm, "end": v(140, 44) * mm});
            skLineSegment(sketch, "E6.0.23.3", {"start": v(140, 44) * mm, "end": v(140, 48) * mm});
            skLineSegment(sketch, "E6.0.24.0", {"start": v(-140, 56) * mm, "end": v(140, 56) * mm});
            skLineSegment(sketch, "E6.0.24.1", {"start": v(-140, 52) * mm, "end": v(-140, 56) * mm});
            skLineSegment(sketch, "E6.0.24.2", {"start": v(-140, 52) * mm, "end": v(140, 52) * mm});
            skLineSegment(sketch, "E6.0.24.3", {"start": v(140, 52) * mm, "end": v(140, 56) * mm});
            skLineSegment(sketch, "E6.0.25.0", {"start": v(-140, 64) * mm, "end": v(140, 64) * mm});
            skLineSegment(sketch, "E6.0.25.1", {"start": v(-140, 60) * mm, "end": v(-140, 64) * mm});
            skLineSegment(sketch, "E6.0.25.2", {"start": v(-140, 60) * mm, "end": v(140, 60) * mm});
            skLineSegment(sketch, "E6.0.25.3", {"start": v(140, 60) * mm, "end": v(140, 64) * mm});
            skLineSegment(sketch, "E6.0.26.0", {"start": v(-140, 72) * mm, "end": v(140, 72) * mm});
            skLineSegment(sketch, "E6.0.26.1", {"start": v(-140, 68) * mm, "end": v(-140, 72) * mm});
            skLineSegment(sketch, "E6.0.26.2", {"start": v(-140, 68) * mm, "end": v(140, 68) * mm});
            skLineSegment(sketch, "E6.0.26.3", {"start": v(140, 68) * mm, "end": v(140, 72) * mm});
            skLineSegment(sketch, "E6.0.27.0", {"start": v(-140, 80) * mm, "end": v(140, 80) * mm});
            skLineSegment(sketch, "E6.0.27.1", {"start": v(-140, 76) * mm, "end": v(-140, 80) * mm});
            skLineSegment(sketch, "E6.0.27.2", {"start": v(-140, 76) * mm, "end": v(140, 76) * mm});
            skLineSegment(sketch, "E6.0.27.3", {"start": v(140, 76) * mm, "end": v(140, 80) * mm});
            skLineSegment(sketch, "E6.0.28.0", {"start": v(-140, 88) * mm, "end": v(140, 88) * mm});
            skLineSegment(sketch, "E6.0.28.1", {"start": v(-140, 84) * mm, "end": v(-140, 88) * mm});
            skLineSegment(sketch, "E6.0.28.2", {"start": v(-140, 84) * mm, "end": v(140, 84) * mm});
            skLineSegment(sketch, "E6.0.28.3", {"start": v(140, 84) * mm, "end": v(140, 88) * mm});
            skLineSegment(sketch, "E6.0.29.0", {"start": v(-140, 96) * mm, "end": v(140, 96) * mm});
            skLineSegment(sketch, "E6.0.29.1", {"start": v(-140, 92) * mm, "end": v(-140, 96) * mm});
            skLineSegment(sketch, "E6.0.29.2", {"start": v(-140, 92) * mm, "end": v(140, 92) * mm});
            skLineSegment(sketch, "E6.0.29.3", {"start": v(140, 92) * mm, "end": v(140, 96) * mm});
            skLineSegment(sketch, "E6.0.30.0", {"start": v(-140, 104) * mm, "end": v(140, 104) * mm});
            skLineSegment(sketch, "E6.0.30.1", {"start": v(-140, 100) * mm, "end": v(-140, 104) * mm});
            skLineSegment(sketch, "E6.0.30.2", {"start": v(-140, 100) * mm, "end": v(140, 100) * mm});
            skLineSegment(sketch, "E6.0.30.3", {"start": v(140, 100) * mm, "end": v(140, 104) * mm});
            skLineSegment(sketch, "E6.0.31.0", {"start": v(-140, 112) * mm, "end": v(140, 112) * mm});
            skLineSegment(sketch, "E6.0.31.1", {"start": v(-140, 108) * mm, "end": v(-140, 112) * mm});
            skLineSegment(sketch, "E6.0.31.2", {"start": v(-140, 108) * mm, "end": v(140, 108) * mm});
            skLineSegment(sketch, "E6.0.31.3", {"start": v(140, 108) * mm, "end": v(140, 112) * mm});
            skLineSegment(sketch, "E6.0.32.0", {"start": v(-140, 120) * mm, "end": v(140, 120) * mm});
            skLineSegment(sketch, "E6.0.32.1", {"start": v(-140, 116) * mm, "end": v(-140, 120) * mm});
            skLineSegment(sketch, "E6.0.32.2", {"start": v(-140, 116) * mm, "end": v(140, 116) * mm});
            skLineSegment(sketch, "E6.0.32.3", {"start": v(140, 116) * mm, "end": v(140, 120) * mm});
            skLineSegment(sketch, "E6.0.33.0", {"start": v(-140, 128) * mm, "end": v(140, 128) * mm});
            skLineSegment(sketch, "E6.0.33.1", {"start": v(-140, 124) * mm, "end": v(-140, 128) * mm});
            skLineSegment(sketch, "E6.0.33.2", {"start": v(-140, 124) * mm, "end": v(140, 124) * mm});
            skLineSegment(sketch, "E6.0.33.3", {"start": v(140, 124) * mm, "end": v(140, 128) * mm});
            skLineSegment(sketch, "E6.0.34.0", {"start": v(-140, 136) * mm, "end": v(140, 136) * mm});
            skLineSegment(sketch, "E6.0.34.1", {"start": v(-140, 132) * mm, "end": v(-140, 136) * mm});
            skLineSegment(sketch, "E6.0.34.2", {"start": v(-140, 132) * mm, "end": v(140, 132) * mm});
            skLineSegment(sketch, "E6.0.34.3", {"start": v(140, 132) * mm, "end": v(140, 136) * mm});
            skLineSegment(sketch, "E6.direction1", {"start": v(-140, -136) * mm, "end": v(-115, -136) * mm, "construction": true});
            skLineSegment(sketch, "E6.direction2", {"start": v(-140, -136) * mm, "end": v(-140, -128) * mm, "construction": true});
            skSolve(sketch);
        }
        {
            var Q0;
            Q0 = qSketchRegion(id + "F6", true);
            extrude(context, id + "F7", {"entities" : qUnion([Q0]), "operationType" : NewBodyOperationType.REMOVE, "oppositeDirection" : true, "depth" : 0.01 * mm, "offsetDistance" : 25 * mm});
        }
        {
            var Q0;
            Q0=qCreatedBy(makeId("Front.planeOp"),FACE);
            var sketch = newSketch(context, id + "F8", { "sketchPlane" : qUnion([Q0])});
            skLineSegment(sketch, "E7", {"start": v(-100, 0) * mm, "end": v(100, 0) * mm});
            skLineSegment(sketch, "E8", {"start": v(100, 0) * mm, "end": v(100, 350) * mm});
            skLineSegment(sketch, "E9", {"start": v(-100, 0) * mm, "end": v(-100, 350) * mm});
            skArc(sketch, "E10", {"start": v(-90, 360) * mm, "mid": v(-97.07, 357.07) * mm, "end": v(-100, 350) * mm});
            skArc(sketch, "E11", {"start": v(100, 350) * mm, "mid": v(97.07, 357.07) * mm, "end": v(90, 360) * mm});
            skLineSegment(sketch, "E12", {"start": v(90, 360) * mm, "end": v(-90, 360) * mm});
            skSolve(sketch);
        }
        {
            var Q0;
            Q0 = qSketchRegion(id + "F8", true);
            extrude(context, id + "F9", {"entities" : qUnion([Q0]), "operationType" : NewBodyOperationType.REMOVE, "endBound" : BoundingType.SYMMETRIC, "oppositeDirection" : true, "depth" : 200 * mm, "offsetDistance" : 25 * mm});
        }
    });
